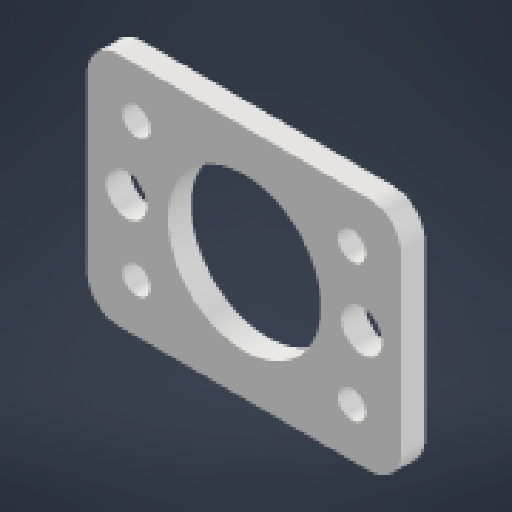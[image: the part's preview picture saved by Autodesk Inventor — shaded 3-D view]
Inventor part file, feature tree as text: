
AUTODESK INVENTOR PART (.ipt)
format: ipt  version: 2024.1 (Build 281209000, 209)  size: 141,312 bytes
history: native  units: mm
features: other x2, extrude x1, sketch x1, reference x1
ambient origin geometry x8: Origin, YZ Plane, XZ Plane, XY Plane, X Axis, Y Axis, Z Axis, Center Point
bodies: Solid1 (feature_tree)
feature tree (5):
  extrude  "Extrusion1"  Depth=3.0mm
  sketch  "Sketch1"  dims[d0=3.5mm d1=19.5mm d2=5.2mm d3=30.0mm d4=3.0mm d5=0.0mm]
  reference  "Reference1"
  other  "Assembly1"
  other  "button_holder:1"
